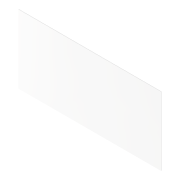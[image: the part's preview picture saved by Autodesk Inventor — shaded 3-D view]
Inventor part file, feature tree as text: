
AUTODESK INVENTOR PART (.ipt)
format: ipt  version: 2022 (Build 260153000, 153)  size: 79,360 bytes
history: native  units: mm
features: extrude x1, plane x1, sketch x1
ambient origin geometry x8: Origin, YZ Plane, XZ Plane, XY Plane, X Axis, Y Axis, Z Axis, Center Point
bodies: Volumenkörper1 (feature_tree)
feature tree (3):
  extrude  "Extrusion1"  Depth=24.0mm
  plane  "Arbeitsebene1"
  sketch  "Skizze1"  dims[d0=50.0mm d1=24.0mm d2=0.2mm d3=0.0mm]
